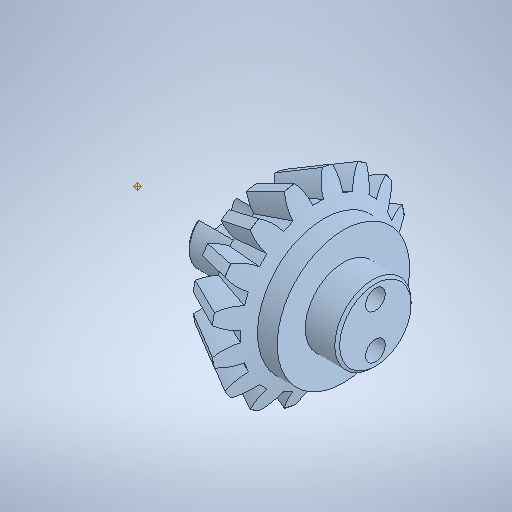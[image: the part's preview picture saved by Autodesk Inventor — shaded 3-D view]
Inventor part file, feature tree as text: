
AUTODESK INVENTOR PART (.ipt)
format: ipt  version: 2025.1 (Build 291241000, 241)  size: 533,504 bytes
history: native  units: in
note: dims shown in document units (in); Inventor stores cm internally (conversion verified against a paired STEP export)
features: sketch x7, plane x6, extrude x3, revolve x2, pattern_circular x1, chamfer x1, hole x1
ambient origin geometry x8: Origin, YZ Plane, XZ Plane, XY Plane, X Axis, Y Axis, Z Axis, Center Point
bodies: Solid1 (feature_tree)
feature tree (21):
  revolve  "Revolution1"  [1 undecoded]
  plane  "Work Plane2"
  plane  "Work Plane5"
  extrude  "Extrusion6"  Depth=0.0945in
  pattern_circular  "Circular Pattern2"  Count=4  [1 undecoded]
  plane  "Work Plane7"
  plane  "Work Plane6"
  sketch  "Sketch11"  dims[d5=0.3937in d9=1.5748in]
  revolve  "Revolution3"  [1 undecoded]
  extrude  "Extrusion8"  Depth=0.3937in
  chamfer  "Chamfer3"  Distance=1.4961in
  hole  "Perçage1"  [1 undecoded]
  extrude  "Extrusion14"  Depth=0.3937in
  sketch  "Sketch1"  dims[d0=3.1496in d1=0.1825in]
  plane  "Work Plane1"
  plane  "Work Plane4"
  sketch  "Sketch8"  dims[d2=0.0787in d3=0.0945in]
  sketch  "Sketch12"  dims[d10=90.0deg d11=0.162in d12=1.5748in]
  sketch  "Sketch13"  dims[d43=0.7043in d47=1.4085in d48=1.4961in d49=0.3543in d50=-0.4359in d51=1.5748in d53=0.0787in d54=0.0691in d56=0.4724in d57=-0.0197in d58=6.2992in d59=360.0deg d63=0.1297in d82=0.0875in d83=-0.0875in d84=1.4086in d89=0.2559in d90=0.315in d91=0.1181in d92=90.0deg d93=0.4567in d94=0.3937in d95=0.0in d96=0.3051in d105=0.0197in d106=0.0787in d107=45.0deg d130=0.1575in d131=0.5292in d132=0.1575in d133=0.2362in d134=0.1575in d135=0.0787in d136=90.0deg d137=0.2362in d138=0.8108in d139=0.1181in d142=0.1772in d143=0.3031in d144=0.5906in d145=0.0in]
  sketch  "Esquisse20"
  sketch  "Esquisse22"
note: 4 required parameter values undecoded (feature->parameter linkage not recoverable at this tier; creation-order binding heuristic only, values carry confidence <= 0.55)